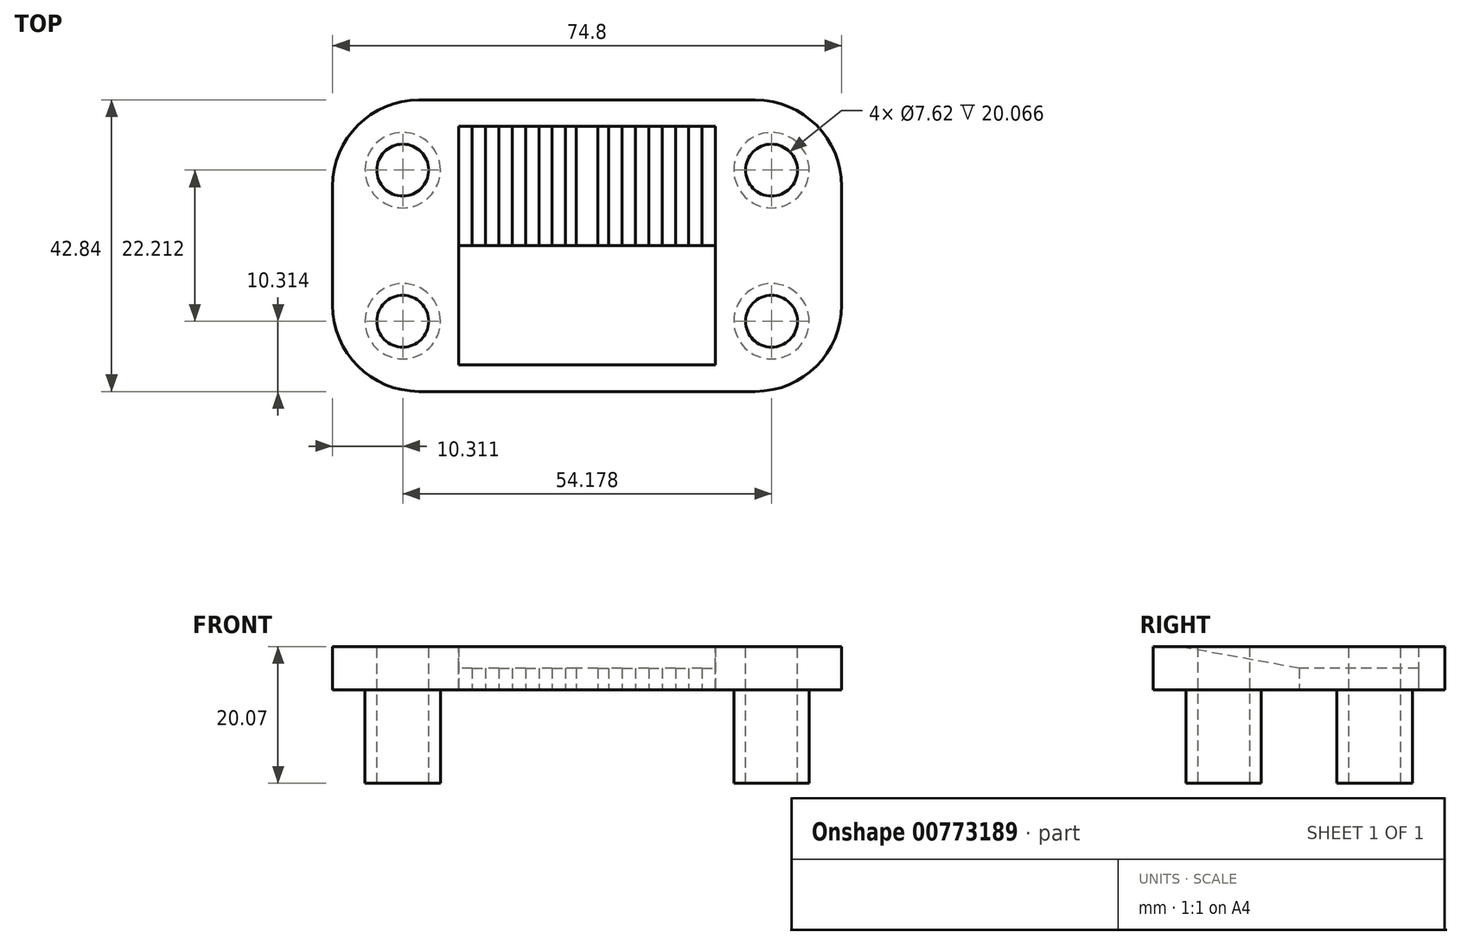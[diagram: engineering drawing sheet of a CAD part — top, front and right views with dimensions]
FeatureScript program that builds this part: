
annotation { "Feature Type Name" : "Feature", "Feature Type Description" : "" }
export const myFeature = defineFeature(function(context is Context, id is Id, definition is map)
    precondition{}
    {
        {
            var Q0;
            Q0=qCreatedBy(makeId("Top.planeOp"),FACE);
            var sketch = newSketch(context, id + "F0", { "sketchPlane" : qUnion([Q0])});
            skLineSegment(sketch, "E0.bottom", {"start": v(24.7, 21.42) * mm, "end": v(0, 21.42) * mm});
            skLineSegment(sketch, "E0.top", {"start": v(24.7, -21.42) * mm, "end": v(0, -21.42) * mm});
            skLineSegment(sketch, "E0.left", {"start": v(37.4, 8.72) * mm, "end": v(37.4, -8.72) * mm});
            skPoint(sketch, "E0.middle", {"position": v(0, 0) * mm});
            skPoint(sketch, "E1", {"position": v(27.09, 11.1) * mm});
            skPoint(sketch, "E2", {"position": v(27.09, -11.1) * mm});
            skArc(sketch, "E3.filletArc", {"start": v(37.4, 8.72) * mm, "mid": v(33.68, 17.7) * mm, "end": v(24.7, 21.42) * mm});
            skArc(sketch, "E4.filletArc", {"start": v(24.7, -21.42) * mm, "mid": v(33.68, -17.7) * mm, "end": v(37.4, -8.72) * mm});
            skCircle(sketch, "E5", {"center": v(27.09, 11.1) * mm, "radius": 5.54 * mm});
            skCircle(sketch, "E6", {"center": v(27.09, -11.1) * mm, "radius": 5.54 * mm});
            skLineSegment(sketch, "E7.bottom", {"start": v(18.85, 17.51) * mm, "end": v(16.89, 17.51) * mm});
            skLineSegment(sketch, "E7.top", {"start": v(18.85, -17.51) * mm, "end": v(0, -17.51) * mm});
            skLineSegment(sketch, "E7.left", {"start": v(18.85, 17.51) * mm, "end": v(18.85, -17.51) * mm});
            skLineSegment(sketch, "E8", {"start": v(0, -21.42) * mm, "end": v(0, -17.51) * mm});
            skLineSegment(sketch, "E9", {"start": v(0, 17.51) * mm, "end": v(0, 21.42) * mm});
            skLineSegment(sketch, "E10", {"start": v(0, 17.51) * mm, "end": v(0, 0) * mm});
            skLineSegment(sketch, "E11", {"start": v(3.18, 0) * mm, "end": v(3.18, 17.51) * mm});
            skLineSegment(sketch, "E12", {"start": v(3.18, 17.51) * mm, "end": v(1.59, 17.51) * mm});
            skLineSegment(sketch, "E13", {"start": v(11.01, 17.51) * mm, "end": v(9.05, 17.51) * mm});
            skLineSegment(sketch, "E14", {"start": v(7.1, 17.51) * mm, "end": v(5.13, 17.51) * mm});
            skLineSegment(sketch, "E15", {"start": v(14.93, 17.51) * mm, "end": v(12.97, 17.51) * mm});
            skLineSegment(sketch, "E16", {"start": v(5.13, 17.51) * mm, "end": v(3.18, 17.51) * mm});
            skLineSegment(sketch, "E17", {"start": v(9.05, 17.51) * mm, "end": v(7.1, 17.51) * mm});
            skLineSegment(sketch, "E18", {"start": v(12.97, 17.51) * mm, "end": v(11.01, 17.51) * mm});
            skLineSegment(sketch, "E19", {"start": v(16.89, 17.51) * mm, "end": v(14.93, 17.51) * mm});
            skLineSegment(sketch, "E20", {"start": v(1.59, 17.51) * mm, "end": v(0, 17.51) * mm});
            skLineSegment(sketch, "E21", {"start": v(1.59, 17.51) * mm, "end": v(1.59, 0) * mm});
            skLineSegment(sketch, "E22", {"start": v(0, 0) * mm, "end": v(1.59, 0) * mm});
            skLineSegment(sketch, "E23", {"start": v(1.59, 0) * mm, "end": v(3.18, 0) * mm});
            skLineSegment(sketch, "E24", {"start": v(3.18, 0) * mm, "end": v(18.85, 0) * mm});
            skLineSegment(sketch, "E25", {"start": v(5.13, 17.51) * mm, "end": v(5.13, 0) * mm});
            skLineSegment(sketch, "E26", {"start": v(7.1, 17.51) * mm, "end": v(7.1, 0) * mm});
            skLineSegment(sketch, "E27", {"start": v(9.05, 17.51) * mm, "end": v(9.05, 0) * mm});
            skLineSegment(sketch, "E28", {"start": v(11.01, 17.51) * mm, "end": v(11.01, 0) * mm});
            skLineSegment(sketch, "E29", {"start": v(12.97, 17.51) * mm, "end": v(12.97, 0) * mm});
            skLineSegment(sketch, "E30", {"start": v(14.93, 17.51) * mm, "end": v(14.93, 0) * mm});
            skLineSegment(sketch, "E31", {"start": v(16.89, 17.51) * mm, "end": v(16.89, 0) * mm});
            skCircle(sketch, "E32", {"center": v(27.09, -11.1) * mm, "radius": 3.81 * mm});
            skCircle(sketch, "E33", {"center": v(27.09, 11.1) * mm, "radius": 3.81 * mm});
            skSolve(sketch);
        }
        {
            var Q0;
            Q0=makeQuery(id+"F0.imprint","IMPRINT",FACE,{"disambiguationData":[TD([[makeQuery(id+"F0.imprint","IMPRINT",EDGE,{"derivedFrom":sQuery(id+"F0.wireOp",EDGE,"E0.bottom")}),1.0]])]});
            extrude(context, id + "F1", {"entities" : qUnion([Q0]), "depth" : 6.35 * mm, "offsetDistance" : 25.4 * mm});
        }
        {
            var Q0;
            Q0=makeQuery(id+"F1.opExtrude","SWEPT_FACE",FACE,{"disambiguationData":[OSD([sQuery(id+"F0.wireOp",EDGE,"E7.left")])]});
            var sketch = newSketch(context, id + "F2", { "sketchPlane" : qUnion([Q0])});
            skLineSegment(sketch, "E34", {"start": v(0, 0) * mm, "end": v(0, 3.18) * mm});
            skLineSegment(sketch, "E35", {"start": v(0, 3.17) * mm, "end": v(17.51, 6.35) * mm});
            skSolve(sketch);
        }
        {
            var Q0;
            {var subQ0=sQuery(id+"F2.wireOp",EDGE,"E34");Q0=makeQuery(id+"F2.imprint","IMPRINT",FACE,{"disambiguationData":[TD([[makeQuery(id+"F2.imprint","IMPRINT",EDGE,{"derivedFrom":subQ0}),-1.0]])]});}
            extrude(context, id + "F3", {"entities" : qUnion([Q0]), "operationType" : NewBodyOperationType.ADD, "depth" : 18.85 * mm, "offsetDistance" : 25.4 * mm});
        }
        {
            var Q0;
            Q0=makeQuery(id+"F0.imprint","IMPRINT",FACE,{"disambiguationData":[TD([[makeQuery(id+"F0.imprint","IMPRINT",EDGE,{"derivedFrom":sQuery(id+"F0.wireOp",EDGE,"E10")}),1.0]])]});
            var Q1;
            {var subQ0=sQuery(id+"F0.wireOp",EDGE,"E11");Q1=makeQuery(id+"F0.imprint","IMPRINT",FACE,{"disambiguationData":[TD([[makeQuery(id+"F0.imprint","IMPRINT",EDGE,{"derivedFrom":subQ0}),-1.0]])]});}
            var Q2;
            Q2=makeQuery(id+"F0.imprint","IMPRINT",FACE,{"disambiguationData":[TD([[makeQuery(id+"F0.imprint","IMPRINT",EDGE,{"derivedFrom":sQuery(id+"F0.wireOp",EDGE,"E17")}),1.0]])]});
            var Q3;
            Q3=makeQuery(id+"F0.imprint","IMPRINT",FACE,{"disambiguationData":[TD([[makeQuery(id+"F0.imprint","IMPRINT",EDGE,{"derivedFrom":sQuery(id+"F0.wireOp",EDGE,"E18")}),1.0]])]});
            var Q4;
            Q4=makeQuery(id+"F0.imprint","IMPRINT",FACE,{"disambiguationData":[TD([[makeQuery(id+"F0.imprint","IMPRINT",EDGE,{"derivedFrom":sQuery(id+"F0.wireOp",EDGE,"E19")}),1.0]])]});
            extrude(context, id + "F4", {"entities" : qUnion([Q0, Q1, Q2, Q3, Q4]), "operationType" : NewBodyOperationType.ADD, "depth" : 3.17 * mm, "offsetDistance" : 25.4 * mm});
        }
        {
            var Q0;
            Q0=makeQuery(id+"F0.imprint","IMPRINT",FACE,{"disambiguationData":[TD([[makeQuery(id+"F0.imprint","IMPRINT",EDGE,{"derivedFrom":sQuery(id+"F0.wireOp",EDGE,"E5")}),1.0]])]});
            var Q1;
            Q1=makeQuery(id+"F0.imprint","IMPRINT",FACE,{"disambiguationData":[TD([[makeQuery(id+"F0.imprint","IMPRINT",EDGE,{"derivedFrom":sQuery(id+"F0.wireOp",EDGE,"E6")}),1.0]])]});
            extrude(context, id + "F5", {"entities" : qUnion([Q0, Q1]), "operationType" : NewBodyOperationType.ADD, "oppositeDirection" : true, "depth" : 13.72 * mm, "offsetDistance" : 25.4 * mm});
        }
        {
            var Q0;
            Q0=makeQuery(id+"F5.opExtrude","CAP_FACE",FACE,{"disambiguationData":[OSD([sQuery(id+"F0.wireOp",EDGE,"E5")])],"isStart":true});
            var Q1;
            Q1=makeQuery(id+"F5.opExtrude","CAP_FACE",FACE,{"disambiguationData":[OSD([sQuery(id+"F0.wireOp",EDGE,"E6")])],"isStart":true});
            extrude(context, id + "F6", {"entities" : qUnion([Q0, Q1]), "depth" : 6.35 * mm, "offsetDistance" : 25.4 * mm});
        }
        {
            var Q0;
            Q0=makeQuery(id+"F5.opExtrude","SWEPT_BODY",BODY,{"disambiguationData":[OSD([sQuery(id+"F0.wireOp",EDGE,"E5"),sQuery(id+"F0.wireOp",EDGE,"E33")])]});
            var Q1;
            Q1=makeQuery(id+"F6.opExtrude","SWEPT_BODY",BODY,{"disambiguationData":[OSD([sQuery(id+"F0.wireOp",EDGE,"E6"),sQuery(id+"F0.wireOp",EDGE,"E32")])]});
            var Q2;
            Q2=makeQuery(id+"F5.opExtrude","SWEPT_BODY",BODY,{"disambiguationData":[OSD([sQuery(id+"F0.wireOp",EDGE,"E6"),sQuery(id+"F0.wireOp",EDGE,"E32")])]});
            var Q3;
            Q3=makeQuery(id+"F1.opExtrude","SWEPT_BODY",BODY,{"disambiguationData":[OSD([sQuery(id+"F0.wireOp",EDGE,"E0.bottom"),sQuery(id+"F0.wireOp",EDGE,"E0.top"),sQuery(id+"F0.wireOp",EDGE,"E0.left"),sQuery(id+"F0.wireOp",EDGE,"E3.filletArc"),sQuery(id+"F0.wireOp",EDGE,"E4.filletArc"),sQuery(id+"F0.wireOp",EDGE,"E5"),sQuery(id+"F0.wireOp",EDGE,"E6"),sQuery(id+"F0.wireOp",EDGE,"E7.bottom"),sQuery(id+"F0.wireOp",EDGE,"E7.top"),sQuery(id+"F0.wireOp",EDGE,"E7.left"),sQuery(id+"F0.wireOp",EDGE,"E8"),sQuery(id+"F0.wireOp",EDGE,"E9"),sQuery(id+"F0.wireOp",EDGE,"E12"),sQuery(id+"F0.wireOp",EDGE,"E13"),sQuery(id+"F0.wireOp",EDGE,"E14"),sQuery(id+"F0.wireOp",EDGE,"E15"),sQuery(id+"F0.wireOp",EDGE,"E16"),sQuery(id+"F0.wireOp",EDGE,"E17"),sQuery(id+"F0.wireOp",EDGE,"E18"),sQuery(id+"F0.wireOp",EDGE,"E19"),sQuery(id+"F0.wireOp",EDGE,"E20")])]});
            var Q4;
            Q4=makeQuery(id+"F6.opExtrude","SWEPT_BODY",BODY,{"disambiguationData":[OSD([sQuery(id+"F0.wireOp",EDGE,"E5"),sQuery(id+"F0.wireOp",EDGE,"E33")])]});
            var Q5;
            Q5=qCreatedBy(makeId("Right.planeOp"),FACE);
            mirror(context, id + "F7", {"operationType" : NewBodyOperationType.ADD, "entities" : qUnion([Q0, Q1, Q2, Q3, Q4]), "mirrorPlane" : qUnion([Q5])});
        }
    });
